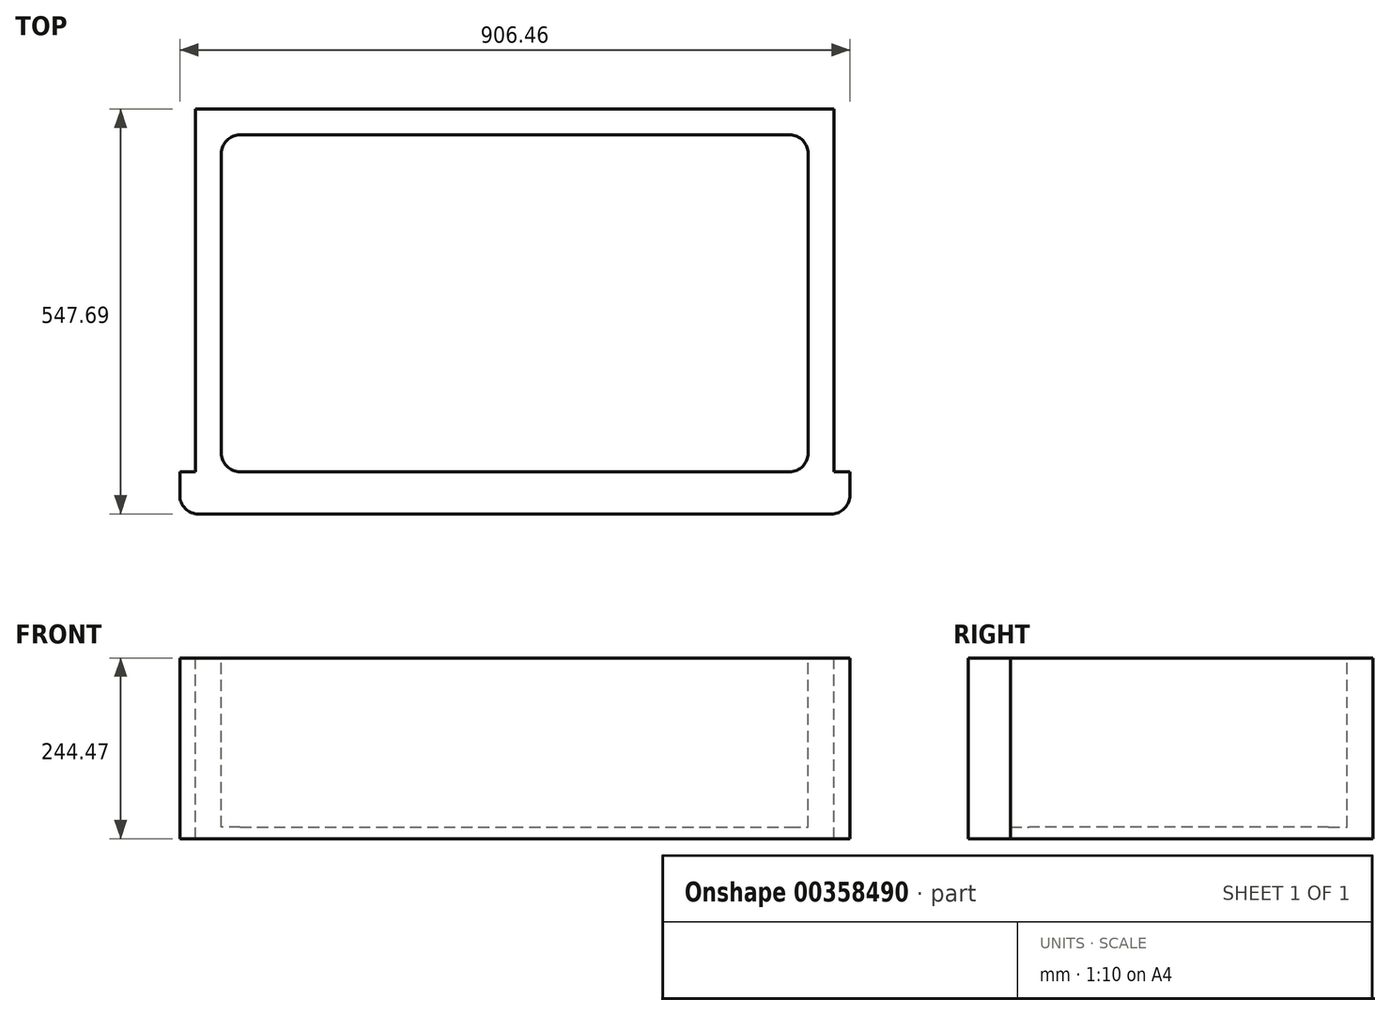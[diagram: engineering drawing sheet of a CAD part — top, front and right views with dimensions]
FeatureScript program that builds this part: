
annotation { "Feature Type Name" : "Feature", "Feature Type Description" : "" }
export const myFeature = defineFeature(function(context is Context, id is Id, definition is map)
    precondition{}
    {
        {
            var Q0;
            Q0=qCreatedBy(makeId("Top.planeOp"),FACE);
            var sketch = newSketch(context, id + "F0", { "sketchPlane" : qUnion([Q0])});
            skLineSegment(sketch, "E0.bottom", {"start": v(-437.76, 201.44) * mm, "end": v(468.7, 201.44) * mm});
            skLineSegment(sketch, "E0.top", {"start": v(-437.76, -346.25) * mm, "end": v(468.7, -346.25) * mm});
            skLineSegment(sketch, "E0.left", {"start": v(-437.76, 201.44) * mm, "end": v(-437.76, -346.25) * mm});
            skLineSegment(sketch, "E0.right", {"start": v(468.7, 201.44) * mm, "end": v(468.7, -346.25) * mm});
            skSolve(sketch);
        }
        {
            var Q0;
            Q0 = qSketchRegion(id + "F0", true);
            extrude(context, id + "F1", {"entities" : qUnion([Q0]), "depth" : 244.47 * mm});
        }
        {
            var Q0;
            Q0=makeQuery(id+"F1.opExtrude","CAP_FACE",FACE,{"disambiguationData":[OSD([sQuery(id+"F0.wireOp",EDGE,"E0.bottom"),sQuery(id+"F0.wireOp",EDGE,"E0.top"),sQuery(id+"F0.wireOp",EDGE,"E0.left"),sQuery(id+"F0.wireOp",EDGE,"E0.right")])],"isStart":false});
            var sketch = newSketch(context, id + "F2", { "sketchPlane" : qUnion([Q0])});
            skLineSegment(sketch, "E1.bottom", {"start": v(-437.76, 201.44) * mm, "end": v(-416.33, 201.44) * mm});
            skLineSegment(sketch, "E1.top", {"start": v(-437.76, -289.1) * mm, "end": v(-416.33, -289.1) * mm});
            skLineSegment(sketch, "E1.left", {"start": v(-437.76, 201.44) * mm, "end": v(-437.76, -289.1) * mm});
            skLineSegment(sketch, "E1.right", {"start": v(-416.33, 201.44) * mm, "end": v(-416.33, -289.1) * mm});
            skLineSegment(sketch, "E2.bottom", {"start": v(468.7, 201.44) * mm, "end": v(447.27, 201.44) * mm});
            skLineSegment(sketch, "E2.top", {"start": v(468.7, -289.1) * mm, "end": v(447.27, -289.1) * mm});
            skLineSegment(sketch, "E2.left", {"start": v(468.7, 201.44) * mm, "end": v(468.7, -289.1) * mm});
            skLineSegment(sketch, "E2.right", {"start": v(447.27, 201.44) * mm, "end": v(447.27, -289.1) * mm});
            skSolve(sketch);
        }
        {
            var Q0;
            Q0 = qSketchRegion(id + "F2", true);
            extrude(context, id + "F3", {"entities" : qUnion([Q0]), "operationType" : NewBodyOperationType.REMOVE, "endBound" : BoundingType.THROUGH_ALL, "oppositeDirection" : true, "depth" : 25.4 * mm});
        }
        {
            var Q0;
            Q0=makeQuery(id+"F1.opExtrude","SWEPT_EDGE",EDGE,{"disambiguationData":[OSD([sQuery(id+"F0.wireOp",EDGE,"E0.top"),sQuery(id+"F0.wireOp",EDGE,"E0.left")])]});
            var Q1;
            Q1=makeQuery(id+"F1.opExtrude","SWEPT_EDGE",EDGE,{"disambiguationData":[OSD([sQuery(id+"F0.wireOp",EDGE,"E0.top"),sQuery(id+"F0.wireOp",EDGE,"E0.right")])]});
            fillet(context, id + "F4", {"entities" : qUnion([Q0, Q1]), "radius" : 25.4 * mm, "tangentPropagation" : true, "allowEdgeOverflow" : false});
        }
        {
            var Q0;
            Q0=makeQuery(id+"F1.opExtrude","CAP_FACE",FACE,{"disambiguationData":[OSD([sQuery(id+"F0.wireOp",EDGE,"E0.bottom"),sQuery(id+"F0.wireOp",EDGE,"E0.top"),sQuery(id+"F0.wireOp",EDGE,"E0.left"),sQuery(id+"F0.wireOp",EDGE,"E0.right")])],"isStart":false});
            var sketch = newSketch(context, id + "F5", { "sketchPlane" : qUnion([Q0])});
            skLineSegment(sketch, "E3.bottom", {"start": v(-381.4, 166.51) * mm, "end": v(412.34, 166.51) * mm});
            skLineSegment(sketch, "E3.top", {"start": v(-381.4, -289.1) * mm, "end": v(412.34, -289.1) * mm});
            skLineSegment(sketch, "E3.left", {"start": v(-381.4, 166.51) * mm, "end": v(-381.4, -289.1) * mm});
            skLineSegment(sketch, "E3.right", {"start": v(412.34, 166.51) * mm, "end": v(412.34, -289.1) * mm});
            skSolve(sketch);
        }
        {
            var Q0;
            Q0 = qSketchRegion(id + "F5", true);
            extrude(context, id + "F6", {"entities" : qUnion([Q0]), "operationType" : NewBodyOperationType.REMOVE, "oppositeDirection" : true, "depth" : 228.6 * mm});
        }
        {
            var Q0;
            Q0=makeQuery(id+"F6.boolean.opBoolean","COPY",EDGE,{"derivedFrom":makeQuery(id+"F6.opExtrude","SWEPT_EDGE",EDGE,{"disambiguationData":[OSD([sQuery(id+"F5.wireOp",EDGE,"E3.bottom"),sQuery(id+"F5.wireOp",EDGE,"E3.right")])]})});
            var Q1;
            Q1=makeQuery(id+"F6.boolean.opBoolean","COPY",EDGE,{"derivedFrom":makeQuery(id+"F6.opExtrude","SWEPT_EDGE",EDGE,{"disambiguationData":[OSD([sQuery(id+"F5.wireOp",EDGE,"E3.bottom"),sQuery(id+"F5.wireOp",EDGE,"E3.left")])]})});
            var Q2;
            Q2=makeQuery(id+"F6.boolean.opBoolean","COPY",EDGE,{"derivedFrom":makeQuery(id+"F6.opExtrude","SWEPT_EDGE",EDGE,{"disambiguationData":[OSD([sQuery(id+"F5.wireOp",EDGE,"E3.top"),sQuery(id+"F5.wireOp",EDGE,"E3.left")])]})});
            var Q3;
            Q3=makeQuery(id+"F6.boolean.opBoolean","COPY",EDGE,{"derivedFrom":makeQuery(id+"F6.opExtrude","SWEPT_EDGE",EDGE,{"disambiguationData":[OSD([sQuery(id+"F5.wireOp",EDGE,"E3.top"),sQuery(id+"F5.wireOp",EDGE,"E3.right")])]})});
            fillet(context, id + "F7", {"entities" : qUnion([Q0, Q1, Q2, Q3]), "radius" : 25.4 * mm, "tangentPropagation" : true, "allowEdgeOverflow" : false});
        }
    });
